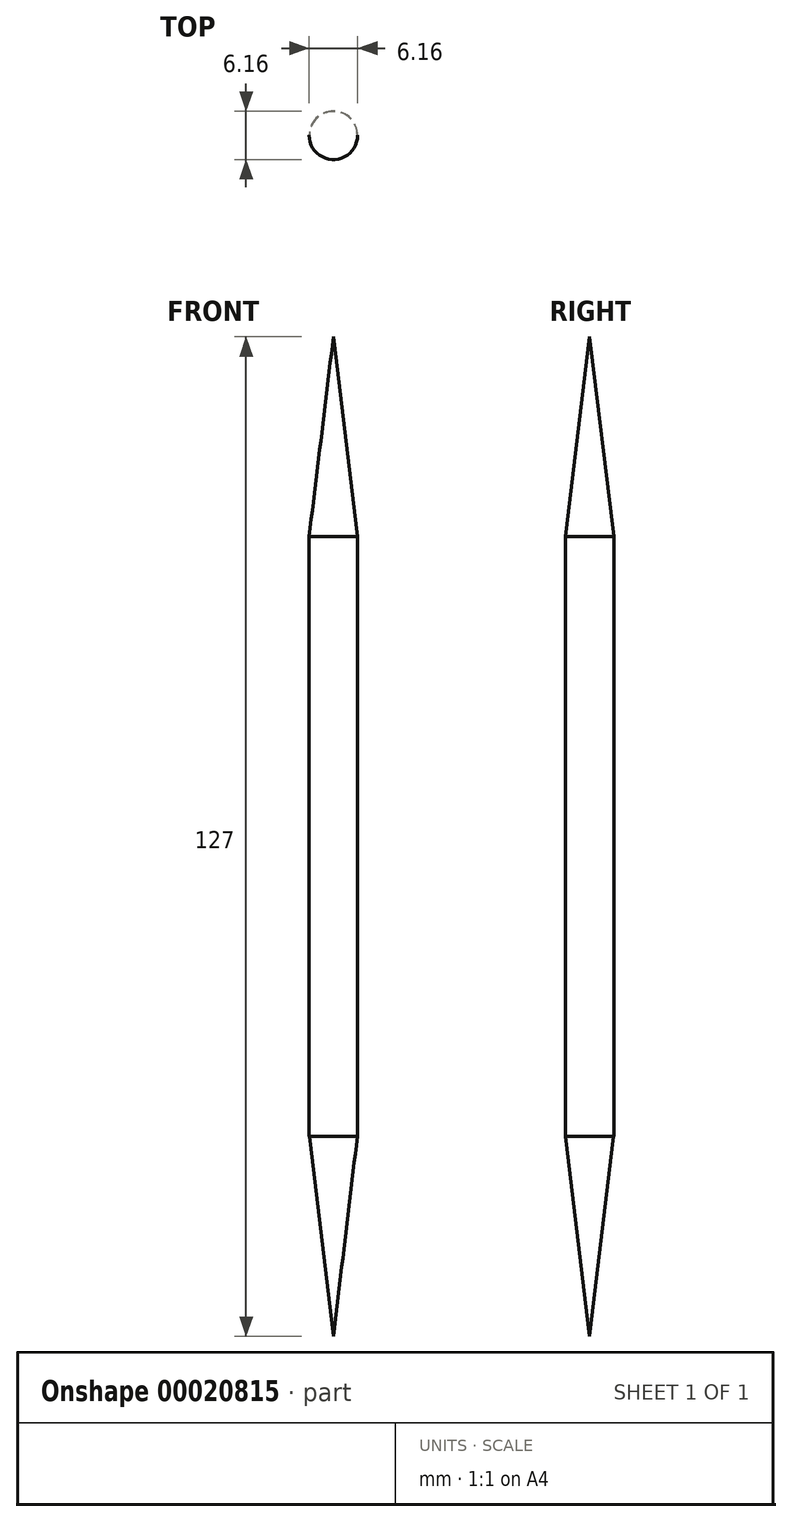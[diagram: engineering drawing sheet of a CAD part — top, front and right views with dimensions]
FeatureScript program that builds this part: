
annotation { "Feature Type Name" : "Feature", "Feature Type Description" : "" }
export const myFeature = defineFeature(function(context is Context, id is Id, definition is map)
    precondition{}
    {
        {
            var Q0;
            Q0=qCreatedBy(makeId("Top.planeOp"),FACE);
            var sketch = newSketch(context, id + "F0", { "sketchPlane" : qUnion([Q0])});
            skCircle(sketch, "E0", {"center": v(0, 0) * mm, "radius": 3.08 * mm});
            skSolve(sketch);
        }
        {
            var Q0;
            Q0=makeQuery(id+"F0.imprint","IMPRINT",FACE,{"disambiguationData":[TD([[makeQuery(id+"F0.imprint","IMPRINT",EDGE,{"derivedFrom":sQuery(id+"F0.wireOp",EDGE,"E0")}),1.0]])]});
            extrude(context, id + "F1", {"entities" : qUnion([Q0]), "endBound" : BoundingType.SYMMETRIC, "depth" : 76.2 * mm});
        }
        {
            var Q0;
            Q0=makeQuery(id+"F1.opExtrude","CAP_FACE",FACE,{"disambiguationData":[OSD([sQuery(id+"F0.wireOp",EDGE,"E0")])],"isStart":false});
            var sketch = newSketch(context, id + "F2", { "sketchPlane" : qUnion([Q0])});
            skCircle(sketch, "E1", {"center": v(0, 0) * mm, "radius": 3.08 * mm});
            skSolve(sketch);
        }
        {
            var Q0;
            Q0=makeQuery(id+"F2.imprint","IMPRINT",FACE,{"disambiguationData":[TD([[makeQuery(id+"F2.imprint","IMPRINT",EDGE,{"derivedFrom":sQuery(id+"F2.wireOp",EDGE,"E1")}),1.0]])]});
            cPlane(context, id + "F3", {"entities" : qUnion([Q0]), "cplaneType" : CPlaneType.OFFSET, "offset" : 25.4 * mm, "width" : 152.4 * mm, "height" : 152.4 * mm});
        }
        {
            var Q0;
            Q0=qCreatedBy(id+"F3.planeOp",FACE);
            var sketch = newSketch(context, id + "F4", { "sketchPlane" : qUnion([Q0])});
            skPoint(sketch, "E2", {"position": v(0, 0) * mm});
            skSolve(sketch);
        }
        {
            var Q1;
            Q1=makeQuery(id+"F2.imprint","IMPRINT",FACE,{"disambiguationData":[TD([[makeQuery(id+"F2.imprint","IMPRINT",EDGE,{"derivedFrom":sQuery(id+"F2.wireOp",EDGE,"E1")}),1.0]])]});
            var Q2;
            Q2=sQuery(id+"F4.wireOp",VERTEX,"E2");
            loft(context, id + "F5", {"operationType" : NewBodyOperationType.ADD, "sheetProfilesArray" : [{ "sheetProfileEntities" : qUnion([Q1]) }, { "sheetProfileEntities" : qUnion([Q2]) }]});
        }
        {
            var Q0;
            Q0=makeQuery(id+"F1.opExtrude","CAP_FACE",FACE,{"disambiguationData":[OSD([sQuery(id+"F0.wireOp",EDGE,"E0")])],"isStart":true});
            var sketch = newSketch(context, id + "F6", { "sketchPlane" : qUnion([Q0])});
            skCircle(sketch, "E3", {"center": v(0, 0) * mm, "radius": 3.04 * mm});
            skSolve(sketch);
        }
        {
            var Q0;
            Q0=makeQuery(id+"F6.imprint","IMPRINT",FACE,{"disambiguationData":[TD([[makeQuery(id+"F6.imprint","IMPRINT",EDGE,{"derivedFrom":sQuery(id+"F6.wireOp",EDGE,"E3")}),1.0]])]});
            cPlane(context, id + "F7", {"entities" : qUnion([Q0]), "cplaneType" : CPlaneType.OFFSET, "offset" : 25.4 * mm, "width" : 152.4 * mm, "height" : 152.4 * mm});
        }
        {
            var Q0;
            Q0=qCreatedBy(id+"F7.planeOp",FACE);
            var sketch = newSketch(context, id + "F8", { "sketchPlane" : qUnion([Q0])});
            skPoint(sketch, "E4", {"position": v(0, 0) * mm});
            skSolve(sketch);
        }
        {
            var Q1;
            Q1=sQuery(id+"F8.wireOp",VERTEX,"E4");
            var Q2;
            Q2=makeQuery(id+"F6.imprint","IMPRINT",FACE,{"disambiguationData":[TD([[makeQuery(id+"F6.imprint","IMPRINT",EDGE,{"derivedFrom":sQuery(id+"F6.wireOp",EDGE,"E3")}),1.0]])]});
            loft(context, id + "F9", {"operationType" : NewBodyOperationType.ADD, "sheetProfilesArray" : [{ "sheetProfileEntities" : qUnion([Q1]) }, { "sheetProfileEntities" : qUnion([Q2]) }]});
        }
    });
